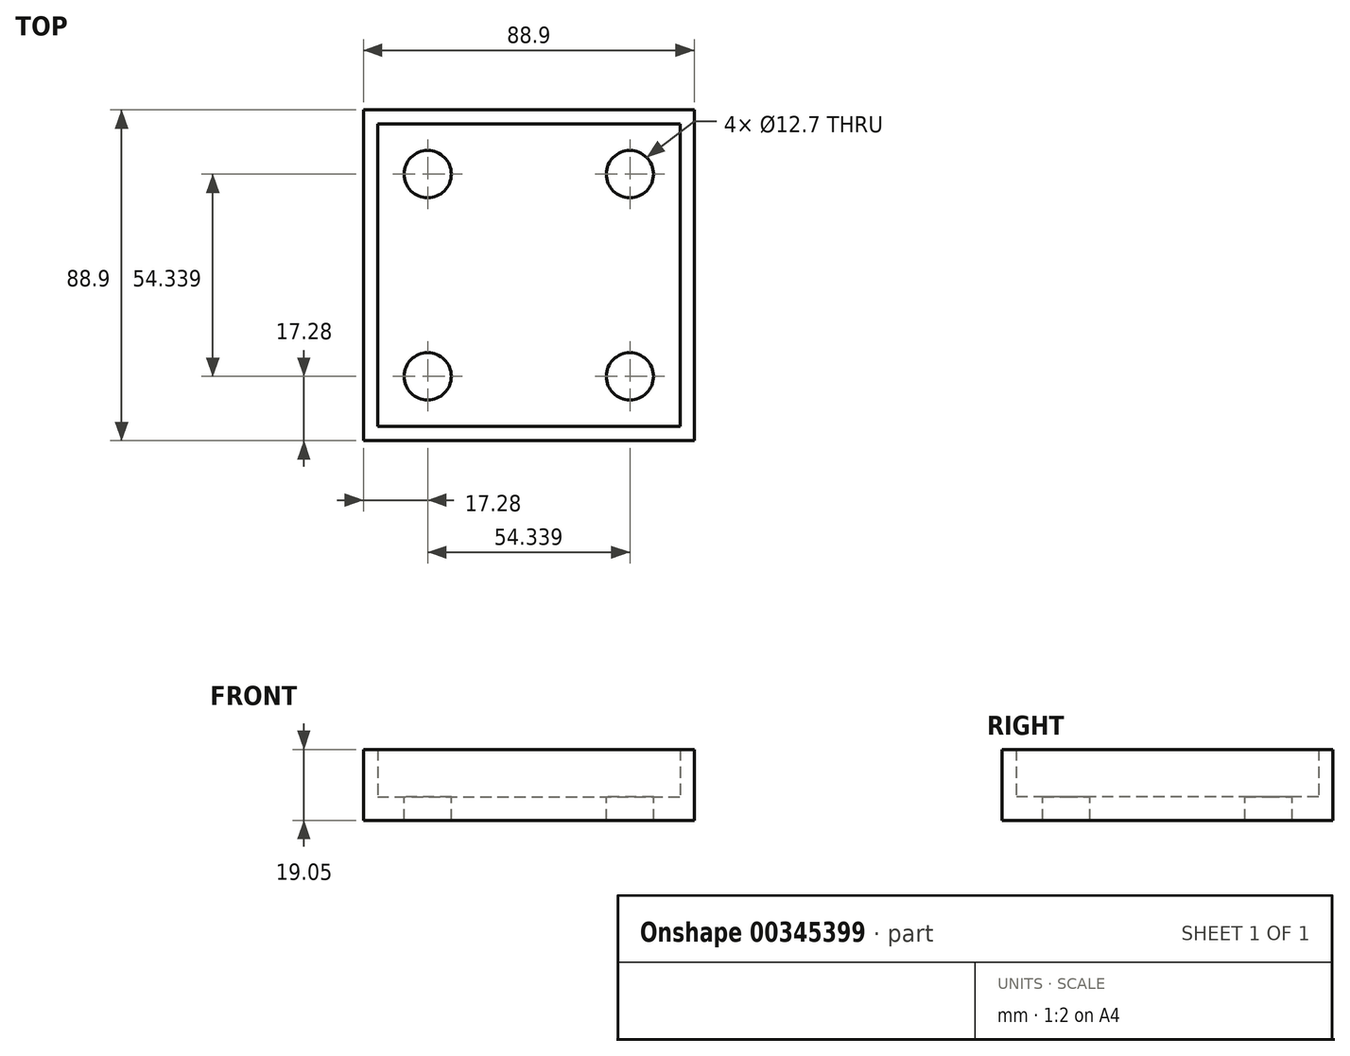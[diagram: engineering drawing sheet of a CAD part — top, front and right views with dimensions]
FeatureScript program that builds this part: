
annotation { "Feature Type Name" : "Feature", "Feature Type Description" : "" }
export const myFeature = defineFeature(function(context is Context, id is Id, definition is map)
    precondition{}
    {
        {
            var Q0;
            Q0=qCreatedBy(makeId("Top.planeOp"),FACE);
            var sketch = newSketch(context, id + "F0", { "sketchPlane" : qUnion([Q0])});
            skLineSegment(sketch, "E0.bottom", {"start": v(0, 0) * mm, "end": v(88.9, 0) * mm});
            skLineSegment(sketch, "E0.top", {"start": v(0, 88.9) * mm, "end": v(88.9, 88.9) * mm});
            skLineSegment(sketch, "E0.left", {"start": v(0, 0) * mm, "end": v(0, 88.9) * mm});
            skLineSegment(sketch, "E0.right", {"start": v(88.9, 0) * mm, "end": v(88.9, 88.9) * mm});
            skSolve(sketch);
        }
        {
            var Q0;
            Q0 = qSketchRegion(id + "F0", true);
            extrude(context, id + "F1", {"entities" : qUnion([Q0]), "depth" : 6.35 * mm});
        }
        {
            var Q0;
            Q0=makeQuery(id+"F1.opExtrude","CAP_FACE",FACE,{"disambiguationData":[OSD([sQuery(id+"F0.wireOp",EDGE,"E0.bottom"),sQuery(id+"F0.wireOp",EDGE,"E0.top"),sQuery(id+"F0.wireOp",EDGE,"E0.left"),sQuery(id+"F0.wireOp",EDGE,"E0.right")])],"isStart":false});
            var sketch = newSketch(context, id + "F2", { "sketchPlane" : qUnion([Q0])});
            skLineSegment(sketch, "E1.bottom", {"start": v(0, 88.9) * mm, "end": v(88.9, 88.9) * mm});
            skLineSegment(sketch, "E1.top", {"start": v(0, 0) * mm, "end": v(88.9, 0) * mm});
            skLineSegment(sketch, "E1.left", {"start": v(0, 88.9) * mm, "end": v(0, 0) * mm});
            skLineSegment(sketch, "E1.right", {"start": v(88.9, 88.9) * mm, "end": v(88.9, 0) * mm});
            skLineSegment(sketch, "E2.bottom", {"start": v(3.81, 85.1) * mm, "end": v(85.1, 85.1) * mm});
            skLineSegment(sketch, "E2.top", {"start": v(3.81, 3.81) * mm, "end": v(85.1, 3.81) * mm});
            skLineSegment(sketch, "E2.left", {"start": v(3.81, 85.1) * mm, "end": v(3.81, 3.81) * mm});
            skLineSegment(sketch, "E2.right", {"start": v(85.1, 85.1) * mm, "end": v(85.1, 3.81) * mm});
            skSolve(sketch);
        }
        {
            var Q0;
            Q0 = qSketchRegion(id + "F2", true);
            extrude(context, id + "F3", {"entities" : qUnion([Q0]), "operationType" : NewBodyOperationType.ADD, "depth" : 12.7 * mm});
        }
        {
            var Q0;
            Q0=makeQuery(id+"F1.opExtrude","CAP_FACE",FACE,{"disambiguationData":[OSD([sQuery(id+"F0.wireOp",EDGE,"E0.bottom"),sQuery(id+"F0.wireOp",EDGE,"E0.top"),sQuery(id+"F0.wireOp",EDGE,"E0.left"),sQuery(id+"F0.wireOp",EDGE,"E0.right")])],"isStart":false});
            var sketch = newSketch(context, id + "F4", { "sketchPlane" : qUnion([Q0])});
            skLineSegment(sketch, "E3", {"start": v(3.81, 85.1) * mm, "end": v(85.1, 3.81) * mm, "construction": true});
            skLineSegment(sketch, "E4", {"start": v(3.81, 3.81) * mm, "end": v(85.1, 85.1) * mm, "construction": true});
            skCircle(sketch, "E5", {"center": v(17.28, 71.62) * mm, "radius": 6.35 * mm});
            skLineSegment(sketch, "E6", {"start": v(3.81, 44.45) * mm, "end": v(85.1, 44.45) * mm, "construction": true});
            skCircle(sketch, "E7.MirrorC", {"center": v(17.28, 17.28) * mm, "radius": 6.35 * mm});
            skLineSegment(sketch, "E8", {"start": v(44.45, 85.1) * mm, "end": v(44.45, 3.8) * mm, "construction": true});
            skCircle(sketch, "E9.MirrorC", {"center": v(71.62, 17.28) * mm, "radius": 6.35 * mm});
            skCircle(sketch, "E10.MirrorC", {"center": v(71.62, 71.62) * mm, "radius": 6.35 * mm});
            skSolve(sketch);
        }
        {
            var Q0;
            Q0 = qSketchRegion(id + "F4", true);
            extrude(context, id + "F5", {"entities" : qUnion([Q0]), "operationType" : NewBodyOperationType.REMOVE, "endBound" : BoundingType.THROUGH_ALL, "oppositeDirection" : true, "depth" : 25.4 * mm});
        }
    });
